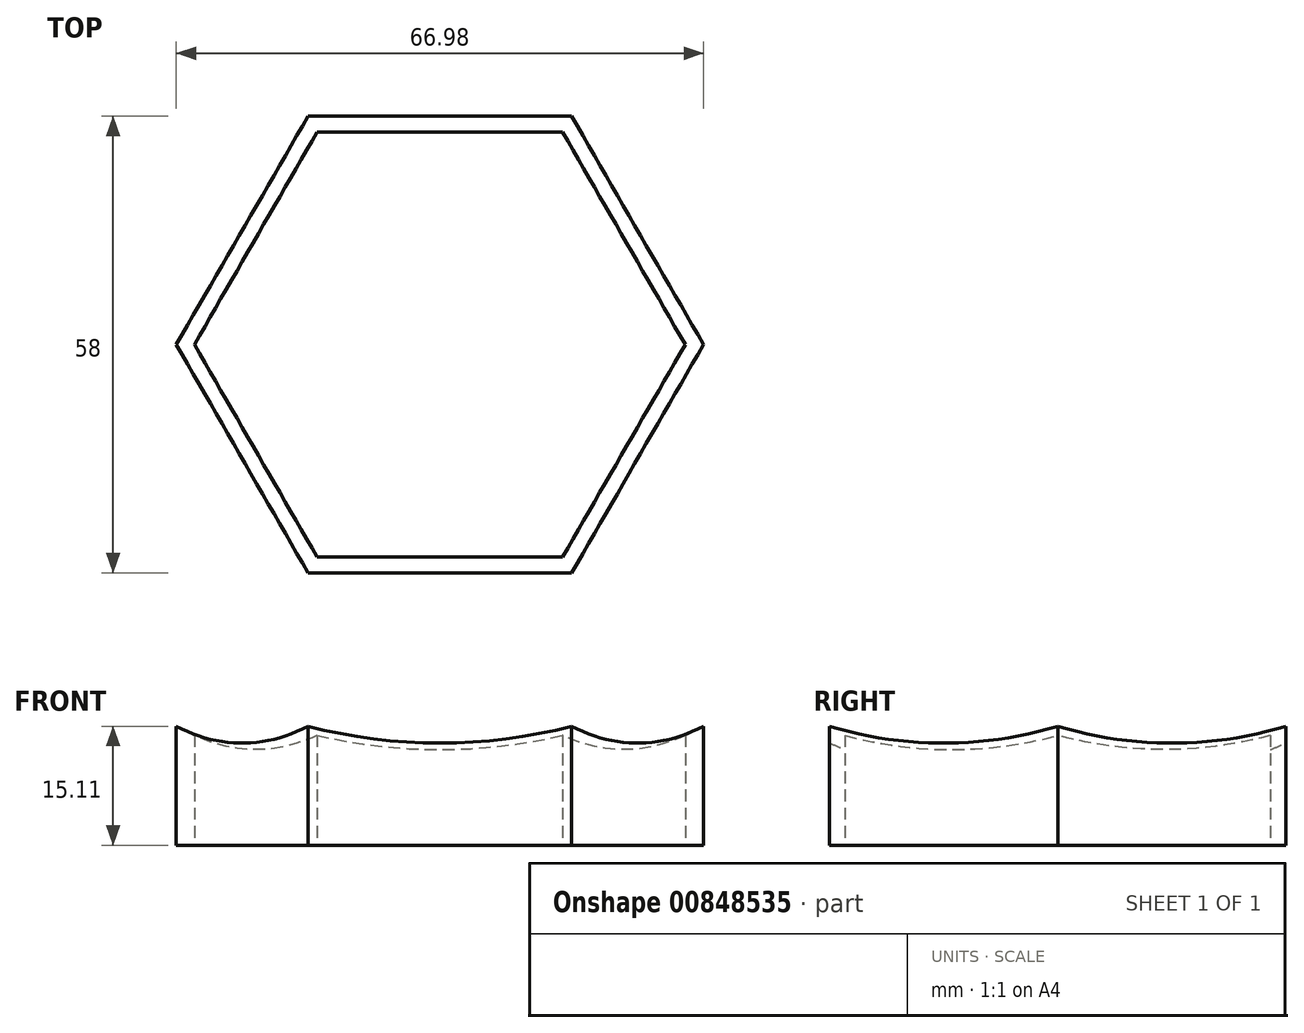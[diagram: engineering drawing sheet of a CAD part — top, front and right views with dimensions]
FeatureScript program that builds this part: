
annotation { "Feature Type Name" : "Feature", "Feature Type Description" : "" }
export const myFeature = defineFeature(function(context is Context, id is Id, definition is map)
    precondition{}
    {
        {
            var Q0;
            Q0=qCreatedBy(makeId("Top.planeOp"),FACE);
            var sketch = newSketch(context, id + "F0", { "sketchPlane" : qUnion([Q0])});
            skCircle(sketch, "E0.cCircle", {"center": v(0, 0) * mm, "radius": 27 * mm, "construction": true});
            skLineSegment(sketch, "E0.0", {"start": v(-15.59, 27) * mm, "end": v(15.59, 27) * mm});
            skLineSegment(sketch, "E0.1", {"start": v(15.59, 27) * mm, "end": v(31.18, 0) * mm});
            skLineSegment(sketch, "E0.2", {"start": v(31.18, 0) * mm, "end": v(15.59, -27) * mm});
            skLineSegment(sketch, "E0.3", {"start": v(15.59, -27) * mm, "end": v(-15.59, -27) * mm});
            skLineSegment(sketch, "E0.4", {"start": v(-15.59, -27) * mm, "end": v(-31.18, 0) * mm});
            skLineSegment(sketch, "E0.5", {"start": v(-31.18, 0) * mm, "end": v(-15.59, 27) * mm});
            skPoint(sketch, "E0.0.midPoint", {"position": v(0, 27) * mm});
            skLineSegment(sketch, "E1.0", {"start": v(-33.49, 0) * mm, "end": v(-16.74, 29) * mm});
            skLineSegment(sketch, "E1.1", {"start": v(16.74, 29) * mm, "end": v(33.49, 0) * mm});
            skLineSegment(sketch, "E1.2", {"start": v(33.49, 0) * mm, "end": v(16.74, -29) * mm});
            skLineSegment(sketch, "E1.3", {"start": v(-16.74, 29) * mm, "end": v(16.74, 29) * mm});
            skLineSegment(sketch, "E1.4", {"start": v(16.74, -29) * mm, "end": v(-16.74, -29) * mm});
            skLineSegment(sketch, "E1.5", {"start": v(-16.74, -29) * mm, "end": v(-33.49, 0) * mm});
            skSolve(sketch);
        }
        {
            var Q0;
            Q0=qCreatedBy(makeId("Front.planeOp"),FACE);
            var sketch = newSketch(context, id + "F1", { "sketchPlane" : qUnion([Q0])});
            skArc(sketch, "E2", {"start": v(0, 6.97) * mm, "mid": v(73.03, 80) * mm, "end": v(0, 153.03) * mm});
            skLineSegment(sketch, "E3", {"start": v(0, 153.03) * mm, "end": v(0, 6.97) * mm});
            skLineSegment(sketch, "E4", {"start": v(0, 158.36) * mm, "end": v(0, 2.4) * mm, "construction": true});
            skSolve(sketch);
        }
        {
            var Q0;
            Q0=makeQuery(id+"F0.imprint","IMPRINT",FACE,{"disambiguationData":[TD([[makeQuery(id+"F0.imprint","IMPRINT",EDGE,{"derivedFrom":sQuery(id+"F0.wireOp",EDGE,"E0.0")}),1.0]])]});
            extrude(context, id + "F2", {"entities" : qUnion([Q0]), "depth" : 25 * mm, "offsetDistance" : 25 * mm});
        }
        {
            var Q0;
            Q0=makeQuery(id+"F1.imprint","IMPRINT",FACE,{"disambiguationData":[TD([[makeQuery(id+"F1.imprint","IMPRINT",EDGE,{"derivedFrom":sQuery(id+"F1.wireOp",EDGE,"E2")}),1.0]])]});
            var Q1;
            Q1=sQuery(id+"F1.wireOp",EDGE,"E4");
            revolve(context, id + "F3", {"operationType" : NewBodyOperationType.REMOVE, "surfaceOperationType" : NewSurfaceOperationType.NEW, "entities" : qUnion([Q0]), "axis" : qUnion([Q1]), "revolveType" : RevolveType.FULL, "oppositeDirection" : true});
        }
    });
